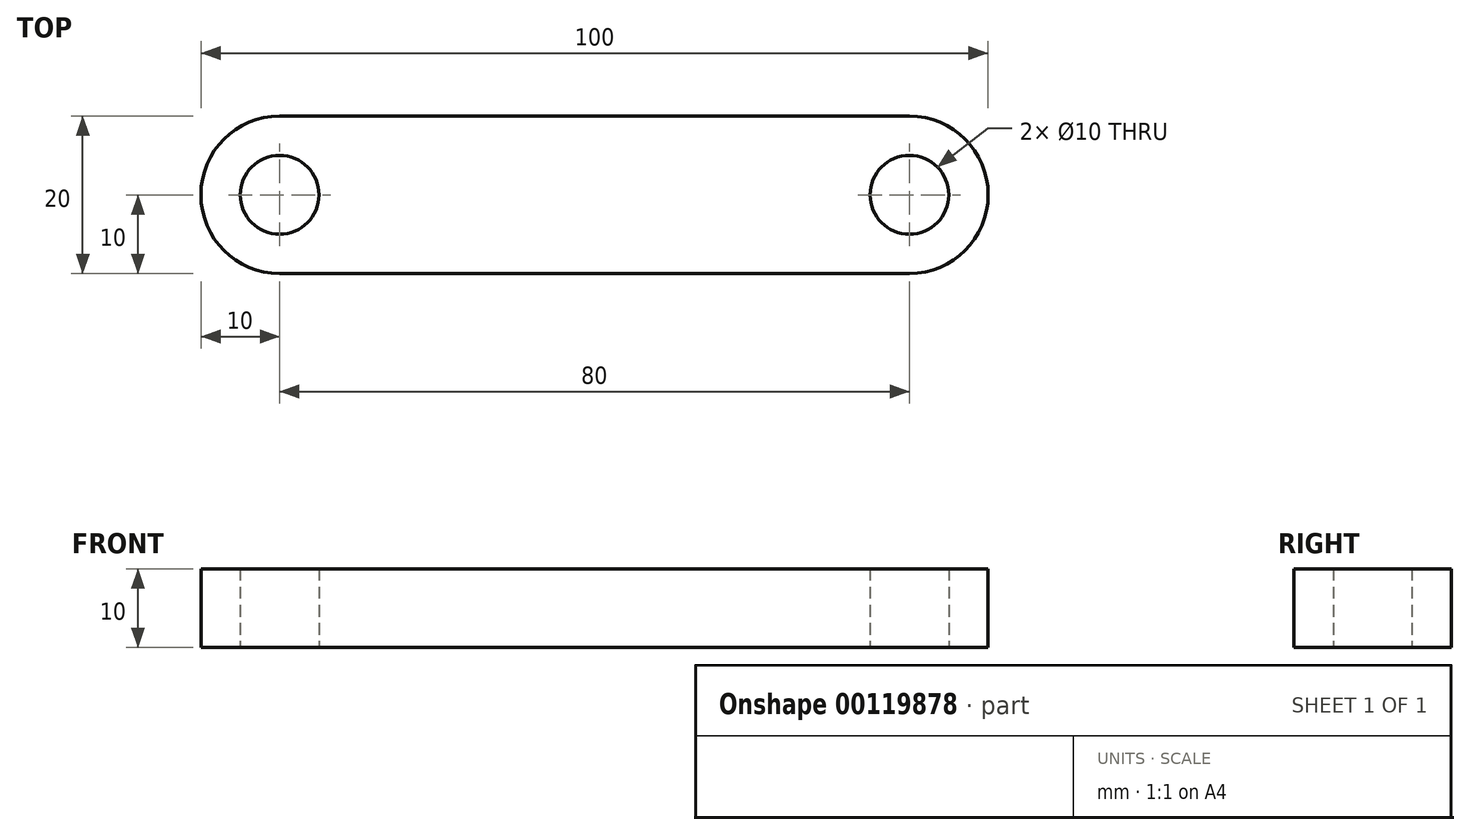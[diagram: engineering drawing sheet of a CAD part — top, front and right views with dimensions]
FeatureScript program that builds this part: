
annotation { "Feature Type Name" : "Feature", "Feature Type Description" : "" }
export const myFeature = defineFeature(function(context is Context, id is Id, definition is map)
    precondition{}
    {
        {
            var Q0;
            Q0=qCreatedBy(makeId("Top.planeOp"),FACE);
            var sketch = newSketch(context, id + "F0", { "sketchPlane" : qUnion([Q0])});
            skCircle(sketch, "E0", {"center": v(-40, 0) * mm, "radius": 5 * mm});
            skCircle(sketch, "E1", {"center": v(40, 0) * mm, "radius": 5 * mm});
            skArc(sketch, "E2", {"start": v(-40, 10) * mm, "mid": v(-50, 0) * mm, "end": v(-40, -10) * mm});
            skLineSegment(sketch, "E3", {"start": v(-40, 10) * mm, "end": v(40, 10) * mm});
            skLineSegment(sketch, "E4", {"start": v(-40, -10) * mm, "end": v(40, -10) * mm});
            skArc(sketch, "E5", {"start": v(40, -10) * mm, "mid": v(50, 0) * mm, "end": v(40, 10) * mm});
            skSolve(sketch);
        }
        {
            var Q0;
            Q0=makeQuery(id+"F0.imprint","IMPRINT",FACE,{"disambiguationData":[TD([[makeQuery(id+"F0.imprint","IMPRINT",EDGE,{"derivedFrom":sQuery(id+"F0.wireOp",EDGE,"E0")}),-1.0]])]});
            extrude(context, id + "F1", {"entities" : qUnion([Q0]), "depth" : 10 * mm});
        }
    });
